# Revit family: Haworth_Riverbend_SeatwithScreen_EU_PRELIMINARY
name_source: partatom
category: Furniture
revit_build: Autodesk Revit 2018 (Build: 20170223_1515(x64)
units: mm (PartAtom-declared; Revit-internal decimal feet)

## family parameters
Always vertical = Yes
Cut with Voids When Loaded = No
OmniClass Number = 23.40.70.14.64.21
OmniClass Title = Systems Furniture
Room Calculation Point = No
Shared = No
Work Plane-Based = No

## types (6) — shared parameters
Actual Height = 137 cm
Assembly Code = E2020200
Description = Haworth - Riverbend - Seater with Screen
Front Finish = Haworth _ Plastic _ Black
Manufacturer = Haworth
Model = SELSSLHX
Revision Number = 1
Size = Verify Final Dim. w/ Haworth
Standard Depths = 88, 82cm
Standard Widths = 74, 144, 174 cm
URL = https://www.haworth.com
URL - Product = https://www.haworth.com
Warranty = http://www.haworth.com

## per-type parameters (varying)
| type | Actual Width | Large | Medium | Seat Width | Small | Trim Finish |
| Single Seater - 52D | 74 cm | No | No | 70 cm | Yes | Haworth _ Plastic _ Black |
| Two Seater - 52D | 144 cm | No | Yes | 140 cm | No | Haworth _ Paint _ Plaster |
| Triple Seater - 52D | 174 cm | Yes | No | 170 cm | No | Haworth _ Plastic _ Black |
| Single Seater - 58D | 74 cm | No | No | 70 cm | Yes | Haworth _ Plastic _ Black |
| Triple Seater - 58D | 174 cm | Yes | No | 170 cm | No | Haworth _ Plastic _ Black |
| Two Seater - 58D | 144 cm | No | Yes | 140 cm | No | Haworth _ Paint _ Plaster |

## geometry (parser evidence)
native form markers: Sweep x13
no freeform markers — native parametric forms only
